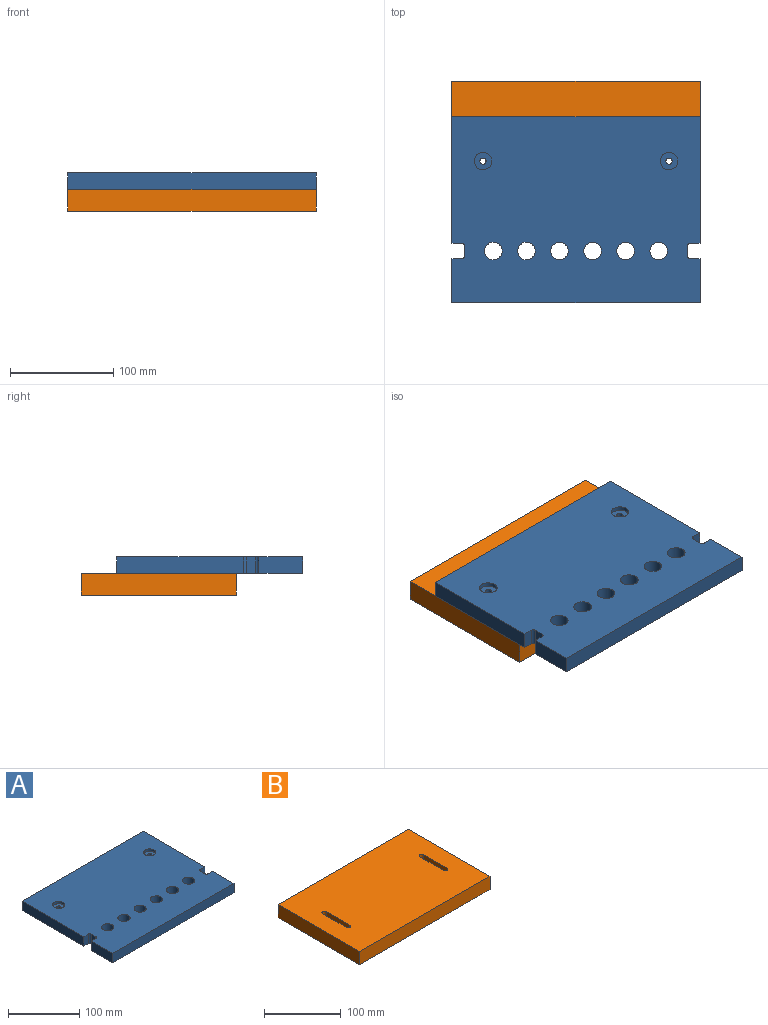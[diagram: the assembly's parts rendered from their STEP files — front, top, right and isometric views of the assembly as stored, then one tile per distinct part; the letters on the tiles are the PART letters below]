
ASSEMBLY  parts=2 mates=2
PART A: 30 faces, bbox 240x180x16 mm
  f0: plane 17x17mm, normal (0,0,1), area 198.7mm2, adj f23,f28
  f1: plane 17x17mm, normal (0,0,1), area 198.7mm2, adj f24,f27
  f2: plane 122.5x16mm, normal (-1,0,0), area 1960mm2, adj f3,f25,f26,f29
  f3: plane 16x9mm, normal (0,-1,0), area 144mm2, adj f2,f4,f26,f29
  f4: cylinder r=3mm len=16mm, axis (0,0,-1), area 75.4mm2, adj f3,f5,f26,f29
  f5: plane 16x9mm, normal (-1,0,0), area 144mm2, adj f4,f6,f26,f29
  f6: cylinder r=3mm len=16mm, axis (0,0,-1), area 75.4mm2, adj f5,f7,f26,f29
  f7: plane 16x9mm, normal (0,1,0), area 144mm2, adj f6,f8,f26,f29
  f8: plane 42.5x16mm, normal (-1,0,0), area 680mm2, adj f7,f9,f26,f29
  f9: plane 240x16mm, normal (0,-1,0), area 3840mm2, adj f8,f10,f26,f29
  f10: plane 42.5x16mm, normal (1,0,0), area 680mm2, adj f9,f11,f26,f29
  f11: plane 16x9mm, normal (0,1,0), area 144mm2, adj f10,f12,f26,f29
  f12: cylinder r=3mm len=16mm, axis (0,0,-1), area 75.4mm2, adj f11,f13,f26,f29
  f13: plane 16x9mm, normal (1,0,0), area 144mm2, adj f12,f14,f26,f29
  f14: cylinder r=3mm len=16mm, axis (0,0,-1), area 75.4mm2, adj f13,f15,f26,f29
  f15: plane 16x9mm, normal (0,-1,0), area 144mm2, adj f14,f16,f26,f29
  f16: plane 122.5x16mm, normal (1,0,0), area 1960mm2, adj f15,f25,f26,f29
  f17: cylinder r=8.5mm len=17mm, axis (0,0,-1), area 854.5mm2, adj f26,f29
  f18: cylinder r=8.5mm len=17mm, axis (0,0,-1), area 854.5mm2, adj f26,f29
  f19: cylinder r=8.5mm len=17mm, axis (0,0,-1), area 854.5mm2, adj f26,f29
  f20: cylinder r=8.5mm len=17mm, axis (0,0,-1), area 854.5mm2, adj f26,f29
  f21: cylinder r=8.5mm len=17mm, axis (0,0,-1), area 854.5mm2, adj f26,f29
  f22: cylinder r=8.5mm len=17mm, axis (0,0,-1), area 854.5mm2, adj f26,f29
  f23: cylinder r=3mm len=12mm, axis (0,0,-1), area 226.2mm2, adj f0,f26
  f24: cylinder r=3mm len=12mm, axis (0,0,-1), area 226.2mm2, adj f1,f26
  f25: plane 240x16mm, normal (0,1,0), area 3840mm2, adj f2,f16,f26,f29
  f26: plane 240x180mm, normal (0,0,-1), area 41429.3mm2, adj f2,f3,f4,f5,f6,f7,f8,f9
  f27: cylinder r=8.5mm len=17mm, axis (0,0,-1), area 213.6mm2, adj f1,f29
  f28: cylinder r=8.5mm len=17mm, axis (0,0,-1), area 213.6mm2, adj f0,f29
  f29: plane 240x180mm, normal (0,0,1), area 41031.9mm2, adj f2,f3,f4,f5,f6,f7,f8,f9
PART B: 14 faces, bbox 240x150x21 mm
  f0: cylinder r=3.5mm len=21mm, axis (0,0,-1), area 230.9mm2, adj f1,f11,f12,f13
  f1: plane 43x21mm, normal (1,0,0), area 903mm2, adj f0,f2,f12,f13
  f2: cylinder r=3.5mm len=21mm, axis (0,0,-1), area 230.9mm2, adj f1,f11,f12,f13
  f3: cylinder r=3.5mm len=21mm, axis (0,0,-1), area 230.9mm2, adj f4,f9,f12,f13
  f4: plane 43x21mm, normal (-1,0,0), area 903mm2, adj f3,f5,f12,f13
  f5: cylinder r=3.5mm len=21mm, axis (0,0,-1), area 230.9mm2, adj f4,f9,f12,f13
  f6: plane 150x21mm, normal (-1,0,0), area 3150mm2, adj f7,f10,f12,f13
  f7: plane 240x21mm, normal (0,-1,0), area 5040mm2, adj f6,f8,f12,f13
  f8: plane 150x21mm, normal (1,0,0), area 3150mm2, adj f7,f10,f12,f13
  f9: plane 43x21mm, normal (1,0,0), area 903mm2, adj f3,f5,f12,f13
  f10: plane 240x21mm, normal (0,1,0), area 5040mm2, adj f6,f8,f12,f13
  f11: plane 43x21mm, normal (-1,0,0), area 903mm2, adj f0,f2,f12,f13
  f12: plane 240x150mm, normal (0,0,1), area 35321mm2, adj f0,f1,f2,f3,f4,f5,f6,f7
  f13: plane 240x150mm, normal (0,0,-1), area 35321mm2, adj f0,f1,f2,f3,f4,f5,f6,f7
PLACE A t=(-79.11,-40.78,124.82)mm
PLACE B t=(-79.11,23.51,103.82)mm
MATE slider B.f12 <-> A.f23  axis (0,0,1) through (-49.11,96.22,124.82)mm
MATE planar B.f12 <-> A.f26  axis (0,0,1) through (40.89,98.54,124.82)mm
